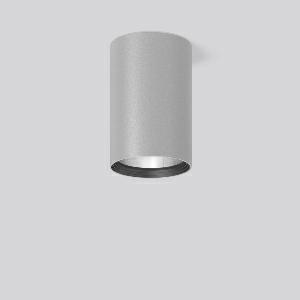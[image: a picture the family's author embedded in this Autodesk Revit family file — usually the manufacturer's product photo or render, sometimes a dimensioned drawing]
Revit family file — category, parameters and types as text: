
# Revit family: heledon_maxi_a_931224_004_1_2a1e
name_source: partatom
category: Lighting Fixtures
units: mm (PartAtom-declared; Revit-internal decimal feet)

## family parameters
Cut with Voids When Loaded = No
Host = Face
Light Source = No
Part Type = Normal
Room Calculation Point = No
Round Connector Dimension = Use Diameter
Shared = No

## types (1)
- HELEDON maxi A (1 x LED Modul 940, 4550 lm, 4000)
    Apparent Load = 35 VA
    Approval mark = CE
    CIE Flux Codes = 100 100 100 100 100
    Color Rendering = 92
    Color Temperature = 4000
    Default Elevation = 1800 mm
    Description = Series: HELEDON maxi
Cylindrical surface-mounted downlight. Housing: die-cast aluminium, powder-coated. Internal ceiling frame polycarbonate with bayonet mounting. Black plastic ring and recessed LED to prevent glare from the side. Optical assembly with reflector made of MIRO-Silver with 98% total light reflection for outstanding efficiency - can be changed without tools. Best colour rendering index Ra>90. Suitable for Ceiling mounting. Easy installation with a separate ceiling frame with bayonet mounting and plug connection. Driver integrated. Connected via plug-in connector. High quality converter without flickering and stroboscopic effect. The following accessories can be mounted without use of tools: interchangeable lenses, decorative glasses, honeycomb louvre, clear and frosted diffusers, white interchangeable plastic ring. 
Colour: silver
Diameter: 123 mm
Height: 183 mm
Lamp: LED
Socket: without socket
Colour temperature: 4000K
Colour rendering index (CRI): 92
System power: 35 W
Rated luminous flux: 4550 lm
Luminous efficiency: 130 lm/W
Control gear: Regulated power supply
Protection class: I
Type of protection: IP 20
    Height = 183 mm
    Lamp = 1 x LED Modul 940
    Lamp Light Flux = 4550 lm
    Lamp count = 1
    Length = 123 mm
    Lifetime = 50000 h
    Luminous efficacy = 130 lm/W
    Manufacturer = RZB
    ModVariant = No
    Model = 931224.004.1
    Mounting Place = Ceiling
    Mounting Type = Surface mounted
    Number of Poles = 1
    OnlyDefault = Yes
    Power Factor = 1
    Product Name = HELEDON maxi A
    Product group = Surface mounted downlights
    ProductGroupID = 302
    Protection Class = Protection class I
    Protection Degree = IP 20
    RLX_Detail_Level = 1
    RLX_Emergency_Light_Flux = 0 lm
    RLX_Emergency_Type = 0
    RLX_Emergency_Type_DB = No
    RlxData = <blob elided: 99601 chars, md5=9c0179e9>
    Socket = socket
    Standby Power = 0 W
    System Light Flux = 4550 lm
    System Power = 35 W
    Type Comments = Product without accessories
    Type Image = 931192.004.jpg
    URL = http://relux.com
    VarID = ---
    Voltage = 230 V
    Voltage Range = 220-240 V
    Weight = 0.00 kg
    Width = 0 mm  [stored 0 ft]

note: [stored X ft] marks values corroborated as IEEE doubles in the binary element streams (Revit-internal decimal feet)

## geometry (parser evidence)
native form markers: Blend x4, Sweep x9
no freeform markers — native parametric forms only
